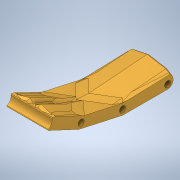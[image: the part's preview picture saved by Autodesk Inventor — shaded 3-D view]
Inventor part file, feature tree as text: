
AUTODESK INVENTOR PART (.ipt)
format: ipt  version: 2020 (Build 240168000, 168)  size: 317,952 bytes
history: native  units: in
note: dims shown in document units (in); Inventor stores cm internally (conversion verified against a paired STEP export)
features: chamfer x11, sketch x6, extrude x5, fillet x3, projected_geometry x1
ambient origin geometry x8: Origin, YZ Plane, XZ Plane, XY Plane, X Axis, Y Axis, Z Axis, Center Point
bodies: Solid1 (feature_tree)
feature tree (26):
  extrude  "Extrusion1"  Depth=1.378in
  extrude  "Extrusion2"  Depth=0.1969in TaperAngle=45.0deg
  chamfer  "Chamfer1"  Distance=0.1969in Angle=45.0deg
  chamfer  "Chamfer2"  Distance=0.1181in Angle=45.0deg
  chamfer  "Chamfer3"  Distance=0.0787in Angle=45.0deg
  chamfer  "Chamfer5"  Distance=1.378in
  extrude  "Extrusion3"  Depth=0.3937in TaperAngle=45.0deg
  chamfer  "Chamfer6"  Distance=0.0394in Angle=45.0deg
  chamfer  "Chamfer8"  Distance=0.0394in Angle=45.0deg
  chamfer  "Chamfer9"  Distance=0.1969in
  chamfer  "Chamfer10"  Distance=0.1969in
  fillet  "Fillet1"  Radius=0.1969in
  fillet  "Fillet2"  Radius=0.1575in
  fillet  "Fillet3"  Radius=0.1575in
  chamfer  "Chamfer11"  Distance=0.3937in
  chamfer  "Chamfer12"  Distance=0.0787in Angle=45.0deg
  extrude  "Extrusion4"  Depth=0.3937in
  chamfer  "Chamfer13"  Distance=0.2047in
  sketch  "Sketch7"  dims[d22=0.1181in d23=1.378in d24=0.0in]
  extrude  "Extrusion5"  Depth=0.3937in
  sketch  "Sketch1"  dims[d0=1.378in d1=0.0in d2=0.5906in]
  sketch  "Sketch2"  dims[d3=1.378in d4=0.0in d5=0.1969in d6=0.689in d7=45.0deg d8=0.1969in d9=0.689in d10=45.0deg d11=0.1181in d12=0.689in d13=45.0deg d17=0.0787in d18=0.689in d19=45.0deg]
  sketch  "Sketch4"  dims[d20=0.1772in]
  sketch  "Sketch5"  dims[d21=0.1772in]
  projected_geometry  "Projected Loop2"
  sketch  "Sketch8"  dims[d25=0.0787in d26=0.689in d27=45.0deg d31=0.0787in d32=0.689in d33=45.0deg d34=0.0394in d35=0.689in d36=45.0deg d37=0.0394in d38=0.689in d39=45.0deg d40=0.1969in d41=0.1969in d42=0.1969in d43=0.1575in d44=0.689in d45=45.0deg d46=0.1575in d47=0.689in d48=45.0deg d49=0.3937in d50=0.0in d51=0.0787in d52=0.0787in d53=45.0deg d54=0.3717in d55=0.2047in d56=0.1102in d57=0.3937in d58=0.0in]
